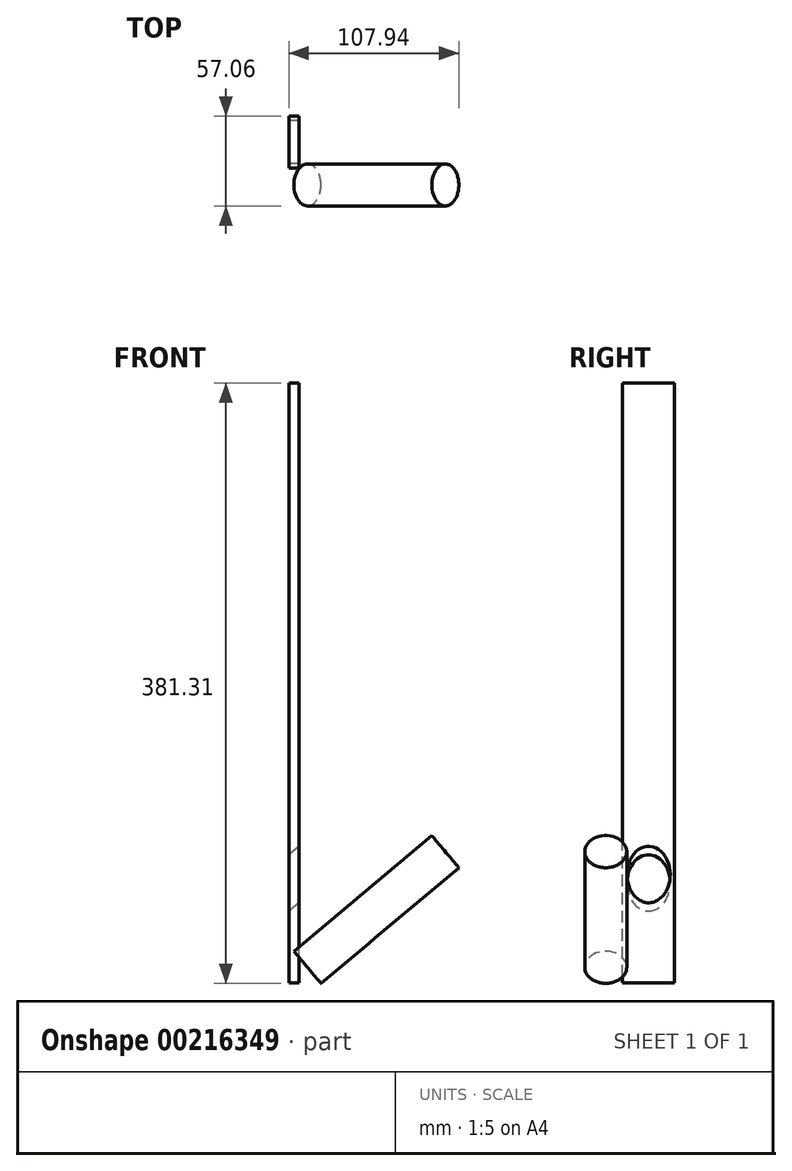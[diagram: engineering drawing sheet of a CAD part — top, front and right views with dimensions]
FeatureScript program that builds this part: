
annotation { "Feature Type Name" : "Feature", "Feature Type Description" : "" }
export const myFeature = defineFeature(function(context is Context, id is Id, definition is map)
    precondition{}
    {
        {
            var Q0;
            Q0=qCreatedBy(makeId("Right.planeOp"),FACE);
            var sketch = newSketch(context, id + "F0", { "sketchPlane" : qUnion([Q0])});
            skLineSegment(sketch, "E0.bottom", {"start": v(16.51, 0) * mm, "end": v(-16.51, 0) * mm});
            skLineSegment(sketch, "E0.top", {"start": v(16.51, 381) * mm, "end": v(-16.5, 381) * mm});
            skLineSegment(sketch, "E0.left", {"start": v(16.51, 0) * mm, "end": v(16.51, 381) * mm});
            skLineSegment(sketch, "E0.right", {"start": v(-16.51, 0) * mm, "end": v(-16.5, 381) * mm});
            skPoint(sketch, "E1", {"position": v(0, 0) * mm});
            skLineSegment(sketch, "E2", {"start": v(-16.5, 63.5) * mm, "end": v(16.51, 63.5) * mm, "construction": true});
            skLineSegment(sketch, "E3", {"start": v(-16.5, 127) * mm, "end": v(16.51, 127) * mm, "construction": true});
            skLineSegment(sketch, "E4", {"start": v(-16.5, 190.5) * mm, "end": v(16.51, 190.5) * mm, "construction": true});
            skLineSegment(sketch, "E5", {"start": v(-16.5, 254) * mm, "end": v(16.51, 254) * mm, "construction": true});
            skLineSegment(sketch, "E6", {"start": v(-16.5, 317.5) * mm, "end": v(16.51, 317.5) * mm, "construction": true});
            skLineSegment(sketch, "E7", {"start": v(0, 0) * mm, "end": v(0, 63.5) * mm, "construction": true});
            skLineSegment(sketch, "E8", {"start": v(0, 63.5) * mm, "end": v(0, 127) * mm, "construction": true});
            skLineSegment(sketch, "E9", {"start": v(0, 127) * mm, "end": v(0, 190.5) * mm, "construction": true});
            skLineSegment(sketch, "E10", {"start": v(0, 190.5) * mm, "end": v(0, 254) * mm, "construction": true});
            skLineSegment(sketch, "E11", {"start": v(0, 254) * mm, "end": v(0, 317.5) * mm, "construction": true});
            skLineSegment(sketch, "E12", {"start": v(0, 317.5) * mm, "end": v(0, 381) * mm, "construction": true});
            skSolve(sketch);
        }
        {
            var Q0;
            Q0 = qSketchRegion(id + "F0", true);
            extrude(context, id + "F1", {"entities" : qUnion([Q0]), "depth" : 6.35 * mm});
        }
        {
            var Q0;
            Q0=sQuery(id+"F0.wireOp",EDGE,"E2");
            cPlane(context, id + "F2", {"entities" : qUnion([Q0]), "cplaneType" : CPlaneType.LINE_ANGLE, "offset" : 25.4 * mm, "angle" : 50 * degree, "width" : 152.4 * mm, "height" : 152.4 * mm});
        }
        {
            var Q0;
            Q0=qCreatedBy(id+"F2.planeOp",FACE);
            var sketch = newSketch(context, id + "F3", { "sketchPlane" : qUnion([Q0])});
            skCircle(sketch, "E13", {"center": v(0, 48.64) * mm, "radius": 13.72 * mm});
            skSolve(sketch);
        }
        {
            var Q0;
            Q0 = qSketchRegion(id + "F3", true);
            extrude(context, id + "F4", {"entities" : qUnion([Q0]), "operationType" : NewBodyOperationType.REMOVE, "endBound" : BoundingType.THROUGH_ALL, "depth" : 25.4 * mm, "hasSecondDirection" : true, "secondDirectionBound" : SecondDirectionBoundingType.THROUGH_ALL, "secondDirectionOppositeDirection" : true, "secondDirectionDepth" : 25.4 * mm});
        }
        {
            var Q0;
            Q0=qCreatedBy(id+"F2.planeOp",FACE);
            var sketch = newSketch(context, id + "F5", { "sketchPlane" : qUnion([Q0])});
            skCircle(sketch, "E14", {"center": v(-27.21, 0) * mm, "radius": 13.34 * mm});
            skSolve(sketch);
        }
        {
            var Q0;
            Q0 = qSketchRegion(id + "F5", true);
            extrude(context, id + "F6", {"entities" : qUnion([Q0]), "depth" : 88.9 * mm, "hasSecondDirection" : true, "secondDirectionOppositeDirection" : true, "secondDirectionDepth" : 25.4 * mm});
        }
    });
